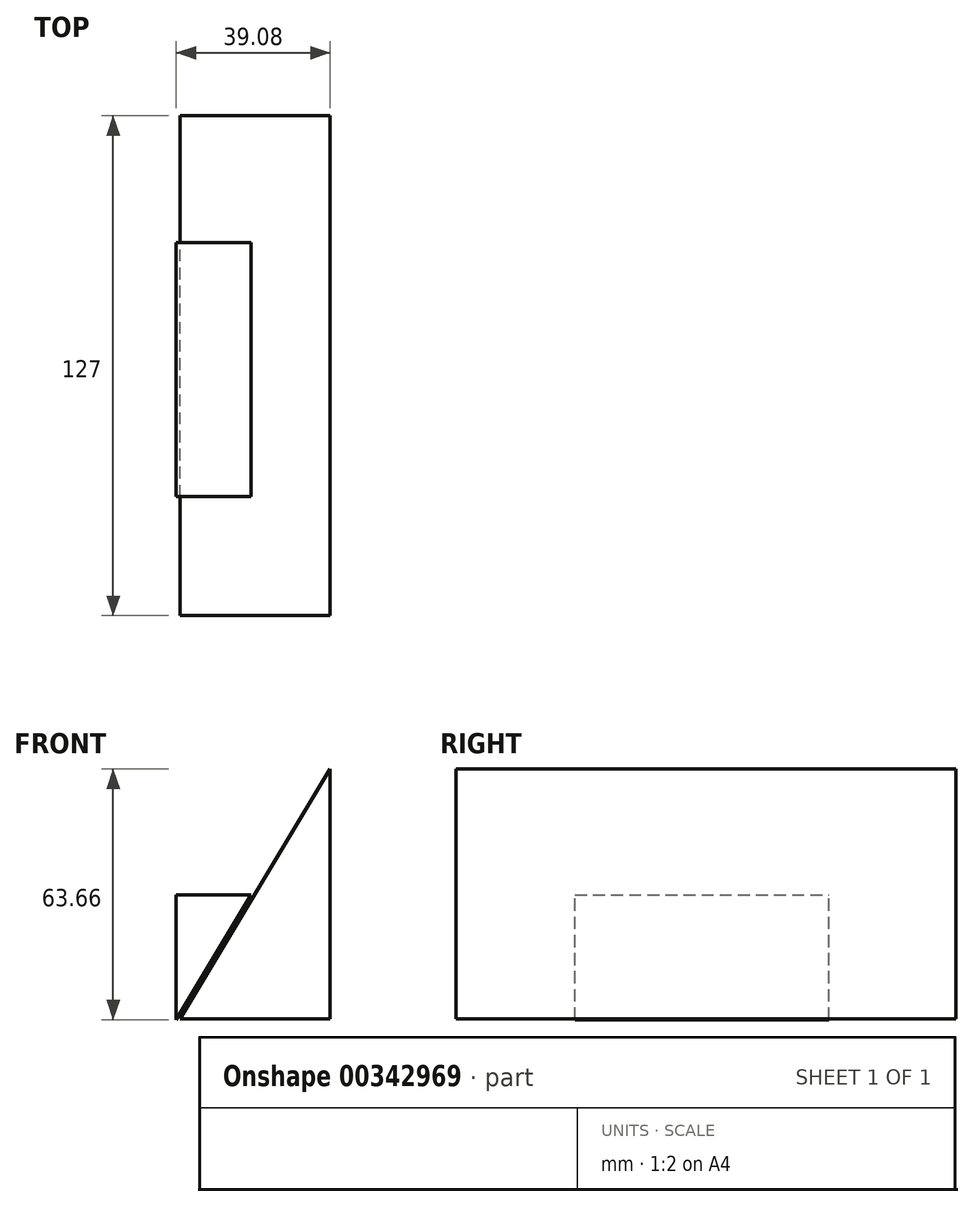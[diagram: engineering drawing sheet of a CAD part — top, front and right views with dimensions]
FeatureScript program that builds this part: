
annotation { "Feature Type Name" : "Feature", "Feature Type Description" : "" }
export const myFeature = defineFeature(function(context is Context, id is Id, definition is map)
    precondition{}
    {
        {
            var Q0;
            Q0=qCreatedBy(makeId("Front.planeOp"),FACE);
            var sketch = newSketch(context, id + "F0", { "sketchPlane" : qUnion([Q0])});
            skLineSegment(sketch, "E0", {"start": v(20.03, -36.56) * mm, "end": v(20.03, 26.94) * mm});
            skLineSegment(sketch, "E1", {"start": v(20.03, -36.56) * mm, "end": v(-18.07, -36.56) * mm});
            skLineSegment(sketch, "E2", {"start": v(-18.07, -36.56) * mm, "end": v(20.03, 26.94) * mm});
            skSolve(sketch);
        }
        {
            var Q0;
            Q0 = qSketchRegion(id + "F0", true);
            extrude(context, id + "F1", {"entities" : qUnion([Q0]), "depth" : 127 * mm});
        }
        {
            var Q0;
            Q0=qCreatedBy(makeId("Front.planeOp"),FACE);
            var sketch = newSketch(context, id + "F2", { "sketchPlane" : qUnion([Q0])});
            skLineSegment(sketch, "E3", {"start": v(-19.05, -36.72) * mm, "end": v(-19.05, -4.97) * mm});
            skPoint(sketch, "E4.end.orphan", {"position": v(0, -4.97) * mm});
            skLineSegment(sketch, "E5", {"start": v(-19.05, -4.97) * mm, "end": v(0, -4.97) * mm});
            skLineSegment(sketch, "E6", {"start": v(-19.05, -36.72) * mm, "end": v(0, -4.97) * mm});
            skSolve(sketch);
        }
        {
            var Q0;
            Q0 = qSketchRegion(id + "F2", true);
            extrude(context, id + "F3", {"entities" : qUnion([Q0]), "depth" : 96.77 * mm, "hasSecondDirection" : true, "secondDirectionOppositeDirection" : false, "secondDirectionDepth" : 32.26 * mm});
        }
    });
